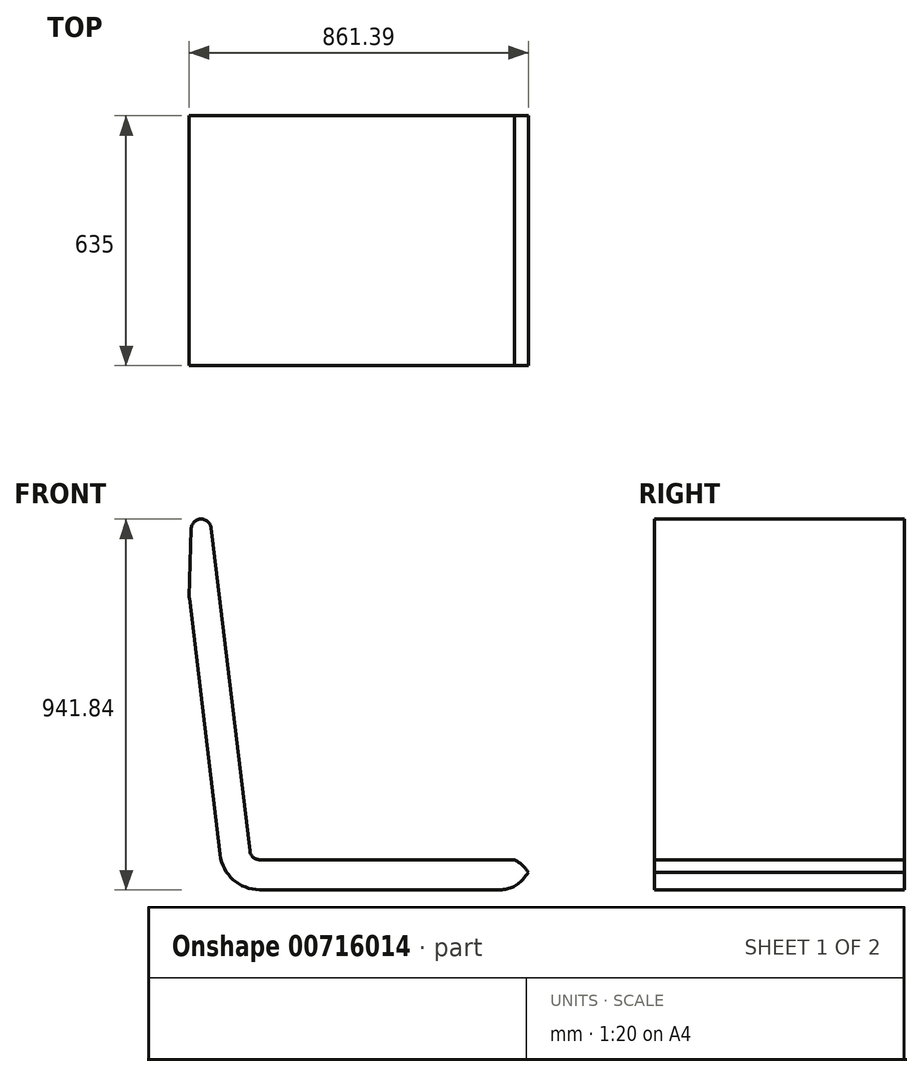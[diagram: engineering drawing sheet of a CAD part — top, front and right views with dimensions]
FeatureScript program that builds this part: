
annotation { "Feature Type Name" : "Feature", "Feature Type Description" : "" }
export const myFeature = defineFeature(function(context is Context, id is Id, definition is map)
    precondition{}
    {
        {
            var Q0;
            Q0=qCreatedBy(makeId("Front.planeOp"),FACE);
            var sketch = newSketch(context, id + "F0", { "sketchPlane" : qUnion([Q0])});
            skLineSegment(sketch, "E0", {"start": v(77.43, 254.2) * mm, "end": v(155.6, -397.22) * mm});
            skLineSegment(sketch, "E1.0", {"start": v(132.76, 432.74) * mm, "end": v(231.25, -388.15) * mm});
            skLineSegment(sketch, "E2", {"start": v(82.15, 430.43) * mm, "end": v(77.26, 257.94) * mm});
            skPoint(sketch, "E3.visualSharp", {"position": v(91.86, 773.55) * mm});
            skArc(sketch, "E3.filletArc", {"start": v(132.76, 432.74) * mm, "mid": v(106.38, 455.09) * mm, "end": v(82.15, 430.43) * mm});
            skPoint(sketch, "E4.visualSharp", {"position": v(77.2, 256.06) * mm});
            skArc(sketch, "E4.filletArc", {"start": v(77.26, 257.94) * mm, "mid": v(77.28, 256.06) * mm, "end": v(77.43, 254.2) * mm});
            skLineSegment(sketch, "E5", {"start": v(256.47, -410.52) * mm, "end": v(902.93, -410.52) * mm});
            skPoint(sketch, "E6.visualSharp", {"position": v(233.93, -410.52) * mm});
            skArc(sketch, "E6.filletArc", {"start": v(231.25, -388.15) * mm, "mid": v(239.61, -404.12) * mm, "end": v(256.47, -410.52) * mm});
            skLineSegment(sketch, "E7.0", {"start": v(256.47, -486.72) * mm, "end": v(867.06, -486.72) * mm});
            skArc(sketch, "E7.1", {"start": v(155.6, -397.22) * mm, "mid": v(189.04, -461.12) * mm, "end": v(256.47, -486.72) * mm});
            skLineSegment(sketch, "E7.2", {"start": v(77.2, 256.06) * mm, "end": v(155.6, -397.22) * mm});
            skLineSegment(sketch, "E8", {"start": v(938.64, -442.34) * mm, "end": v(927.61, -456.78) * mm});
            skPoint(sketch, "E9.visualSharp", {"position": v(904.74, -486.72) * mm});
            skArc(sketch, "E9.filletArc", {"start": v(867.06, -486.72) * mm, "mid": v(900.83, -478.83) * mm, "end": v(927.61, -456.78) * mm});
            skPoint(sketch, "E10.orphan", {"position": v(183.12, -626.61) * mm});
            skArc(sketch, "E11", {"start": v(938.64, -442.34) * mm, "mid": v(923.1, -423.84) * mm, "end": v(902.93, -410.52) * mm});
            skSolve(sketch);
        }
        {
            var Q0;
            Q0=makeQuery(id+"F0.imprint","IMPRINT",FACE,{"disambiguationData":[TD([[makeQuery(id+"F0.imprint","IMPRINT",EDGE,{"derivedFrom":sQuery(id+"F0.wireOp",EDGE,"E1.0")}),-1.0]])]});
            extrude(context, id + "F1", {"entities" : qUnion([Q0]), "depth" : 635 * mm, "offsetDistance" : 25.4 * mm});
        }
    });
